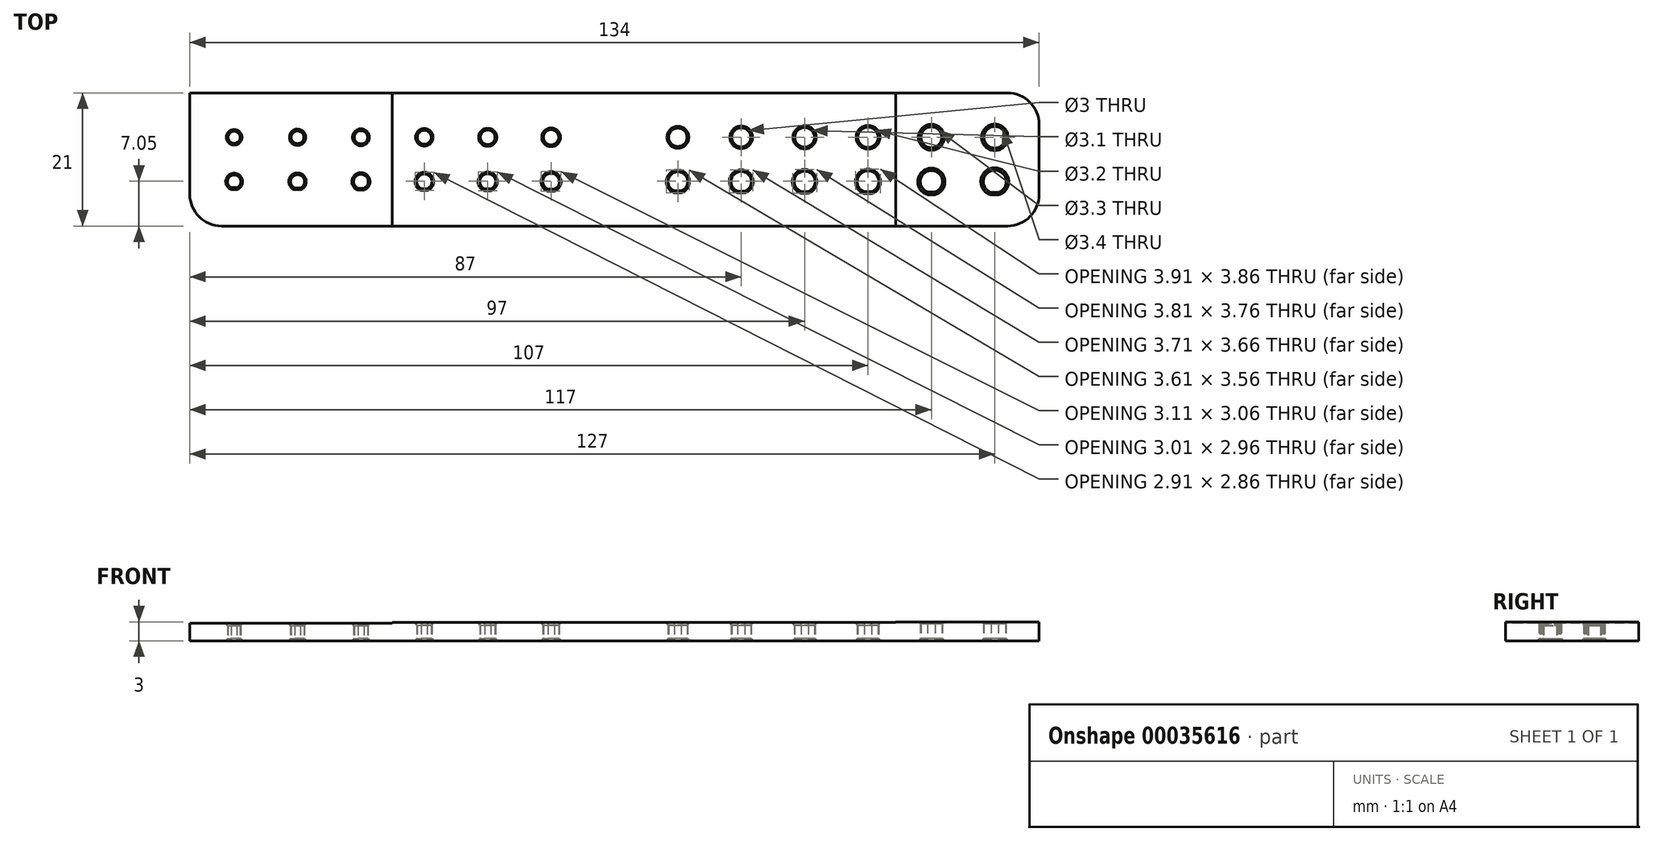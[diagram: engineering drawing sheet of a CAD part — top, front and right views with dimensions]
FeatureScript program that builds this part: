
annotation { "Feature Type Name" : "Feature", "Feature Type Description" : "" }
export const myFeature = defineFeature(function(context is Context, id is Id, definition is map)
    precondition{}
    {
        {
            var Q0;
            Q0=qCreatedBy(makeId("Top.planeOp"),FACE);
            var sketch = newSketch(context, id + "F0", { "sketchPlane" : qUnion([Q0])});
            skPoint(sketch, "E0.rect.middle", {"position": v(0, 0) * mm});
            skCircle(sketch, "E1", {"center": v(-50, 0) * mm, "radius": 1 * mm});
            skCircle(sketch, "E2", {"center": v(-40, 0) * mm, "radius": 1.05 * mm});
            skCircle(sketch, "E3", {"center": v(-30, 0) * mm, "radius": 1.1 * mm});
            skCircle(sketch, "E4", {"center": v(-20, 0) * mm, "radius": 1.15 * mm});
            skCircle(sketch, "E5", {"center": v(-10, 0) * mm, "radius": 1.2 * mm});
            skCircle(sketch, "E6", {"center": v(10, 0) * mm, "radius": 1.45 * mm});
            skCircle(sketch, "E7", {"center": v(20, 0) * mm, "radius": 1.5 * mm});
            skCircle(sketch, "E8", {"center": v(30, 0) * mm, "radius": 1.55 * mm});
            skCircle(sketch, "E9", {"center": v(40, 0) * mm, "radius": 1.6 * mm});
            skCircle(sketch, "E10", {"center": v(50, 0) * mm, "radius": 1.65 * mm});
            skCircle(sketch, "E11", {"center": v(60, 0) * mm, "radius": 1.7 * mm});
            skCircle(sketch, "E12", {"center": v(-60, 0) * mm, "radius": 0.95 * mm});
            skCircle(sketch, "E13", {"center": v(-30, -7) * mm, "radius": 1.2 * mm});
            skCircle(sketch, "E14", {"center": v(-20, -7) * mm, "radius": 1.25 * mm});
            skCircle(sketch, "E15", {"center": v(-10, -7) * mm, "radius": 1.3 * mm});
            skCircle(sketch, "E16", {"center": v(-40, -7) * mm, "radius": 1.15 * mm});
            skCircle(sketch, "E17", {"center": v(-50, -7) * mm, "radius": 1.1 * mm});
            skCircle(sketch, "E18", {"center": v(10, -7) * mm, "radius": 1.55 * mm});
            skPoint(sketch, "E19.rect.middle", {"position": v(0, -7) * mm});
            skCircle(sketch, "E20", {"center": v(20, -7) * mm, "radius": 1.6 * mm});
            skCircle(sketch, "E21", {"center": v(30, -7) * mm, "radius": 1.65 * mm});
            skCircle(sketch, "E22", {"center": v(40, -7) * mm, "radius": 1.7 * mm});
            skCircle(sketch, "E23", {"center": v(50, -7) * mm, "radius": 1.75 * mm});
            skCircle(sketch, "E24", {"center": v(60, -7) * mm, "radius": 1.8 * mm});
            skCircle(sketch, "E25", {"center": v(-60, -7) * mm, "radius": 1.05 * mm});
            skLineSegment(sketch, "E26.bottom", {"start": v(-67, 7) * mm, "end": v(67, 7) * mm});
            skLineSegment(sketch, "E26.top", {"start": v(-67, -14) * mm, "end": v(67, -14) * mm});
            skLineSegment(sketch, "E26.left", {"start": v(-67, 7) * mm, "end": v(-67, -14) * mm});
            skLineSegment(sketch, "E26.right", {"start": v(67, 7) * mm, "end": v(67, -14) * mm});
            skLineSegment(sketch, "E27", {"start": v(-60.45, -7.95) * mm, "end": v(-59.55, -7.95) * mm});
            skLineSegment(sketch, "E28", {"start": v(-50.46, -8) * mm, "end": v(-49.54, -8) * mm});
            skLineSegment(sketch, "E29", {"start": v(-40.47, -8.05) * mm, "end": v(-39.53, -8.05) * mm});
            skLineSegment(sketch, "E30", {"start": v(-30.48, -8.1) * mm, "end": v(-29.52, -8.1) * mm});
            skLineSegment(sketch, "E31", {"start": v(-20.49, -8.15) * mm, "end": v(-19.51, -8.15) * mm});
            skLineSegment(sketch, "E32", {"start": v(-10.5, -8.2) * mm, "end": v(-9.5, -8.2) * mm});
            skLineSegment(sketch, "E33", {"start": v(9.45, -8.45) * mm, "end": v(10.55, -8.45) * mm});
            skLineSegment(sketch, "E34", {"start": v(19.44, -8.5) * mm, "end": v(20.56, -8.5) * mm});
            skLineSegment(sketch, "E35", {"start": v(29.43, -8.55) * mm, "end": v(30.57, -8.55) * mm});
            skLineSegment(sketch, "E36", {"start": v(39.43, -8.6) * mm, "end": v(40.57, -8.6) * mm});
            skLineSegment(sketch, "E37", {"start": v(49.42, -8.65) * mm, "end": v(50.58, -8.65) * mm});
            skLineSegment(sketch, "E38", {"start": v(59.4, -8.7) * mm, "end": v(60.6, -8.7) * mm});
            skSolve(sketch);
        }
        {
            var Q0;
            {var subQ0=sQuery(id+"F0.wireOp",EDGE,"E27");Q0=makeQuery(id+"F0.imprint","IMPRINT",FACE,{"disambiguationData":[TD([[makeQuery(id+"F0.imprint","IMPRINT",EDGE,{"derivedFrom":subQ0}),-1.0]])]});}
            var Q1;
            {var subQ0=sQuery(id+"F0.wireOp",EDGE,"E28");Q1=makeQuery(id+"F0.imprint","IMPRINT",FACE,{"disambiguationData":[TD([[makeQuery(id+"F0.imprint","IMPRINT",EDGE,{"derivedFrom":subQ0}),-1.0]])]});}
            var Q2;
            {var subQ0=sQuery(id+"F0.wireOp",EDGE,"E29");Q2=makeQuery(id+"F0.imprint","IMPRINT",FACE,{"disambiguationData":[TD([[makeQuery(id+"F0.imprint","IMPRINT",EDGE,{"derivedFrom":subQ0}),-1.0]])]});}
            var Q3;
            {var subQ0=sQuery(id+"F0.wireOp",EDGE,"E30");Q3=makeQuery(id+"F0.imprint","IMPRINT",FACE,{"disambiguationData":[TD([[makeQuery(id+"F0.imprint","IMPRINT",EDGE,{"derivedFrom":subQ0}),-1.0]])]});}
            var Q4;
            {var subQ0=sQuery(id+"F0.wireOp",EDGE,"E31");Q4=makeQuery(id+"F0.imprint","IMPRINT",FACE,{"disambiguationData":[TD([[makeQuery(id+"F0.imprint","IMPRINT",EDGE,{"derivedFrom":subQ0}),-1.0]])]});}
            var Q5;
            {var subQ0=sQuery(id+"F0.wireOp",EDGE,"E32");Q5=makeQuery(id+"F0.imprint","IMPRINT",FACE,{"disambiguationData":[TD([[makeQuery(id+"F0.imprint","IMPRINT",EDGE,{"derivedFrom":subQ0}),-1.0]])]});}
            var Q6;
            {var subQ0=sQuery(id+"F0.wireOp",EDGE,"E33");Q6=makeQuery(id+"F0.imprint","IMPRINT",FACE,{"disambiguationData":[TD([[makeQuery(id+"F0.imprint","IMPRINT",EDGE,{"derivedFrom":subQ0}),-1.0]])]});}
            var Q7;
            {var subQ0=sQuery(id+"F0.wireOp",EDGE,"E34");Q7=makeQuery(id+"F0.imprint","IMPRINT",FACE,{"disambiguationData":[TD([[makeQuery(id+"F0.imprint","IMPRINT",EDGE,{"derivedFrom":subQ0}),-1.0]])]});}
            var Q8;
            Q8=makeQuery(id+"F0.imprint","IMPRINT",FACE,{"disambiguationData":[TD([[makeQuery(id+"F0.imprint","IMPRINT",EDGE,{"derivedFrom":sQuery(id+"F0.wireOp",EDGE,"E1")}),-1.0]])]});
            var Q9;
            {var subQ0=sQuery(id+"F0.wireOp",EDGE,"E35");Q9=makeQuery(id+"F0.imprint","IMPRINT",FACE,{"disambiguationData":[TD([[makeQuery(id+"F0.imprint","IMPRINT",EDGE,{"derivedFrom":subQ0}),-1.0]])]});}
            var Q10;
            {var subQ0=sQuery(id+"F0.wireOp",EDGE,"E36");Q10=makeQuery(id+"F0.imprint","IMPRINT",FACE,{"disambiguationData":[TD([[makeQuery(id+"F0.imprint","IMPRINT",EDGE,{"derivedFrom":subQ0}),-1.0]])]});}
            var Q11;
            {var subQ0=sQuery(id+"F0.wireOp",EDGE,"E37");Q11=makeQuery(id+"F0.imprint","IMPRINT",FACE,{"disambiguationData":[TD([[makeQuery(id+"F0.imprint","IMPRINT",EDGE,{"derivedFrom":subQ0}),-1.0]])]});}
            var Q12;
            {var subQ0=sQuery(id+"F0.wireOp",EDGE,"E38");Q12=makeQuery(id+"F0.imprint","IMPRINT",FACE,{"disambiguationData":[TD([[makeQuery(id+"F0.imprint","IMPRINT",EDGE,{"derivedFrom":subQ0}),-1.0]])]});}
            extrude(context, id + "F1", {"entities" : qUnion([Q0, Q1, Q2, Q3, Q4, Q5, Q6, Q7, Q8, Q9, Q10, Q11, Q12]), "depth" : 3 * mm});
        }
        {
            var Q0;
            Q0=makeQuery(id+"F1.opExtrude","CAP_FACE",FACE,{"disambiguationData":[OSD([sQuery(id+"F0.wireOp",EDGE,"E0.rect.bottom"),sQuery(id+"F0.wireOp",EDGE,"E0.rect.top"),sQuery(id+"F0.wireOp",EDGE,"E0.rect.left"),sQuery(id+"F0.wireOp",EDGE,"E0.rect.right"),sQuery(id+"F0.wireOp",EDGE,"E1"),sQuery(id+"F0.wireOp",EDGE,"E2"),sQuery(id+"F0.wireOp",EDGE,"E3"),sQuery(id+"F0.wireOp",EDGE,"E4"),sQuery(id+"F0.wireOp",EDGE,"E5"),sQuery(id+"F0.wireOp",EDGE,"E6"),sQuery(id+"F0.wireOp",EDGE,"E7"),sQuery(id+"F0.wireOp",EDGE,"E8"),sQuery(id+"F0.wireOp",EDGE,"E9"),sQuery(id+"F0.wireOp",EDGE,"E10"),sQuery(id+"F0.wireOp",EDGE,"E11"),sQuery(id+"F0.wireOp",EDGE,"E12")])],"isStart":false});
            var sketch = newSketch(context, id + "F2", { "sketchPlane" : qUnion([Q0])});
            skLineSegment(sketch, "E39.rect.bottom", {"start": v(44.35, -20.42) * mm, "end": v(-71, -20.42) * mm});
            skLineSegment(sketch, "E39.rect.top", {"start": v(44.35, 10.73) * mm, "end": v(-71, 10.73) * mm});
            skLineSegment(sketch, "E39.rect.left", {"start": v(44.35, -20.42) * mm, "end": v(44.35, 10.73) * mm});
            skLineSegment(sketch, "E39.rect.right", {"start": v(-71, -20.42) * mm, "end": v(-71, 10.73) * mm});
            skPoint(sketch, "E39.rect.middle", {"position": v(-13.32, -4.84) * mm});
            skSolve(sketch);
        }
        {
            var Q0;
            Q0 = qSketchRegion(id + "F2", true);
            extrude(context, id + "F3", {"entities" : qUnion([Q0]), "operationType" : NewBodyOperationType.REMOVE, "oppositeDirection" : true, "depth" : .1 * mm});
        }
        {
            var Q0;
            Q0=makeQuery(id+"F3.boolean.opBoolean","COPY",FACE,{"derivedFrom":makeQuery(id+"F3.opExtrude","CAP_FACE",FACE,{"disambiguationData":[OSD([sQuery(id+"F2.wireOp",EDGE,"E39.rect.bottom"),sQuery(id+"F2.wireOp",EDGE,"E39.rect.top"),sQuery(id+"F2.wireOp",EDGE,"E39.rect.left"),sQuery(id+"F2.wireOp",EDGE,"E39.rect.right")])],"isStart":false})});
            var sketch = newSketch(context, id + "F4", { "sketchPlane" : qUnion([Q0])});
            skLineSegment(sketch, "E40.bottom", {"start": v(-72.45, 11.13) * mm, "end": v(-35.06, 11.13) * mm});
            skLineSegment(sketch, "E40.top", {"start": v(-72.45, -20.3) * mm, "end": v(-35.06, -20.3) * mm});
            skLineSegment(sketch, "E40.left", {"start": v(-72.45, 11.13) * mm, "end": v(-72.45, -20.3) * mm});
            skLineSegment(sketch, "E40.right", {"start": v(-35.06, 11.13) * mm, "end": v(-35.06, -20.3) * mm});
            skSolve(sketch);
        }
        {
            var Q0;
            Q0 = qSketchRegion(id + "F4", true);
            extrude(context, id + "F5", {"entities" : qUnion([Q0]), "operationType" : NewBodyOperationType.REMOVE, "oppositeDirection" : true, "depth" : .1 * mm});
        }
        {
            var Q0;
            Q0=makeQuery(id+"F1.opExtrude","SWEPT_EDGE",EDGE,{"disambiguationData":[OSD([sQuery(id+"F0.wireOp",EDGE,"E26.top"),sQuery(id+"F0.wireOp",EDGE,"E26.left")])]});
            var Q1;
            Q1=makeQuery(id+"F1.opExtrude","SWEPT_EDGE",EDGE,{"disambiguationData":[OSD([sQuery(id+"F0.wireOp",EDGE,"E26.top"),sQuery(id+"F0.wireOp",EDGE,"E26.right")])]});
            var Q2;
            Q2=makeQuery(id+"F1.opExtrude","SWEPT_EDGE",EDGE,{"disambiguationData":[OSD([sQuery(id+"F0.wireOp",EDGE,"E26.bottom"),sQuery(id+"F0.wireOp",EDGE,"E26.right")])]});
            fillet(context, id + "F6", {"entities" : qUnion([Q0, Q1, Q2]), "radius" : 5 * mm, "tangentPropagation" : true, "allowEdgeOverflow" : false});
        }
        {
            var Q0;
            Q0=makeQuery(id+"F5.boolean.opBoolean","INTERSECT",EDGE,{"derivedFrom":[makeQuery(id+"F1.opExtrude","SWEPT_FACE",FACE,{"disambiguationData":[OSD([sQuery(id+"F0.wireOp",EDGE,"E12")])]}),makeQuery(id+"F5.opExtrude","CAP_FACE",FACE,{"disambiguationData":[OSD([sQuery(id+"F4.wireOp",EDGE,"E40.bottom"),sQuery(id+"F4.wireOp",EDGE,"E40.top"),sQuery(id+"F4.wireOp",EDGE,"E40.left"),sQuery(id+"F4.wireOp",EDGE,"E40.right")])],"isStart":false})]});
            var Q1;
            Q1=makeQuery(id+"F5.boolean.opBoolean","INTERSECT",EDGE,{"derivedFrom":[makeQuery(id+"F1.opExtrude","SWEPT_FACE",FACE,{"disambiguationData":[OSD([sQuery(id+"F0.wireOp",EDGE,"E1")])]}),makeQuery(id+"F5.opExtrude","CAP_FACE",FACE,{"disambiguationData":[OSD([sQuery(id+"F4.wireOp",EDGE,"E40.bottom"),sQuery(id+"F4.wireOp",EDGE,"E40.top"),sQuery(id+"F4.wireOp",EDGE,"E40.left"),sQuery(id+"F4.wireOp",EDGE,"E40.right")])],"isStart":false})]});
            var Q2;
            Q2=makeQuery(id+"F5.boolean.opBoolean","INTERSECT",EDGE,{"derivedFrom":[makeQuery(id+"F1.opExtrude","SWEPT_FACE",FACE,{"disambiguationData":[OSD([sQuery(id+"F0.wireOp",EDGE,"E25")])]}),makeQuery(id+"F5.opExtrude","CAP_FACE",FACE,{"disambiguationData":[OSD([sQuery(id+"F4.wireOp",EDGE,"E40.bottom"),sQuery(id+"F4.wireOp",EDGE,"E40.top"),sQuery(id+"F4.wireOp",EDGE,"E40.left"),sQuery(id+"F4.wireOp",EDGE,"E40.right")])],"isStart":false})]});
            var Q3;
            Q3=makeQuery(id+"F5.boolean.opBoolean","INTERSECT",EDGE,{"derivedFrom":[makeQuery(id+"F1.opExtrude","SWEPT_FACE",FACE,{"disambiguationData":[OSD([sQuery(id+"F0.wireOp",EDGE,"E27")])]}),makeQuery(id+"F5.opExtrude","CAP_FACE",FACE,{"disambiguationData":[OSD([sQuery(id+"F4.wireOp",EDGE,"E40.bottom"),sQuery(id+"F4.wireOp",EDGE,"E40.top"),sQuery(id+"F4.wireOp",EDGE,"E40.left"),sQuery(id+"F4.wireOp",EDGE,"E40.right")])],"isStart":false})]});
            var Q4;
            Q4=makeQuery(id+"F5.boolean.opBoolean","INTERSECT",EDGE,{"derivedFrom":[makeQuery(id+"F1.opExtrude","SWEPT_FACE",FACE,{"disambiguationData":[OSD([sQuery(id+"F0.wireOp",EDGE,"E28")])]}),makeQuery(id+"F5.opExtrude","CAP_FACE",FACE,{"disambiguationData":[OSD([sQuery(id+"F4.wireOp",EDGE,"E40.bottom"),sQuery(id+"F4.wireOp",EDGE,"E40.top"),sQuery(id+"F4.wireOp",EDGE,"E40.left"),sQuery(id+"F4.wireOp",EDGE,"E40.right")])],"isStart":false})]});
            var Q5;
            Q5=makeQuery(id+"F5.boolean.opBoolean","INTERSECT",EDGE,{"derivedFrom":[makeQuery(id+"F1.opExtrude","SWEPT_FACE",FACE,{"disambiguationData":[OSD([sQuery(id+"F0.wireOp",EDGE,"E17")])]}),makeQuery(id+"F5.opExtrude","CAP_FACE",FACE,{"disambiguationData":[OSD([sQuery(id+"F4.wireOp",EDGE,"E40.bottom"),sQuery(id+"F4.wireOp",EDGE,"E40.top"),sQuery(id+"F4.wireOp",EDGE,"E40.left"),sQuery(id+"F4.wireOp",EDGE,"E40.right")])],"isStart":false})]});
            var Q6;
            Q6=makeQuery(id+"F5.boolean.opBoolean","INTERSECT",EDGE,{"derivedFrom":[makeQuery(id+"F1.opExtrude","SWEPT_FACE",FACE,{"disambiguationData":[OSD([sQuery(id+"F0.wireOp",EDGE,"E2")])]}),makeQuery(id+"F5.opExtrude","CAP_FACE",FACE,{"disambiguationData":[OSD([sQuery(id+"F4.wireOp",EDGE,"E40.bottom"),sQuery(id+"F4.wireOp",EDGE,"E40.top"),sQuery(id+"F4.wireOp",EDGE,"E40.left"),sQuery(id+"F4.wireOp",EDGE,"E40.right")])],"isStart":false})]});
            var Q7;
            Q7=makeQuery(id+"F5.boolean.opBoolean","INTERSECT",EDGE,{"derivedFrom":[makeQuery(id+"F1.opExtrude","SWEPT_FACE",FACE,{"disambiguationData":[OSD([sQuery(id+"F0.wireOp",EDGE,"E29")])]}),makeQuery(id+"F5.opExtrude","CAP_FACE",FACE,{"disambiguationData":[OSD([sQuery(id+"F4.wireOp",EDGE,"E40.bottom"),sQuery(id+"F4.wireOp",EDGE,"E40.top"),sQuery(id+"F4.wireOp",EDGE,"E40.left"),sQuery(id+"F4.wireOp",EDGE,"E40.right")])],"isStart":false})]});
            var Q8;
            Q8=makeQuery(id+"F5.boolean.opBoolean","INTERSECT",EDGE,{"derivedFrom":[makeQuery(id+"F1.opExtrude","SWEPT_FACE",FACE,{"disambiguationData":[OSD([sQuery(id+"F0.wireOp",EDGE,"E16")])]}),makeQuery(id+"F5.opExtrude","CAP_FACE",FACE,{"disambiguationData":[OSD([sQuery(id+"F4.wireOp",EDGE,"E40.bottom"),sQuery(id+"F4.wireOp",EDGE,"E40.top"),sQuery(id+"F4.wireOp",EDGE,"E40.left"),sQuery(id+"F4.wireOp",EDGE,"E40.right")])],"isStart":false})]});
            var Q9;
            Q9=makeQuery(id+"F3.boolean.opBoolean","INTERSECT",EDGE,{"derivedFrom":[makeQuery(id+"F1.opExtrude","SWEPT_FACE",FACE,{"disambiguationData":[OSD([sQuery(id+"F0.wireOp",EDGE,"E3")])]}),makeQuery(id+"F3.opExtrude","CAP_FACE",FACE,{"disambiguationData":[OSD([sQuery(id+"F2.wireOp",EDGE,"E39.rect.bottom"),sQuery(id+"F2.wireOp",EDGE,"E39.rect.top"),sQuery(id+"F2.wireOp",EDGE,"E39.rect.left"),sQuery(id+"F2.wireOp",EDGE,"E39.rect.right")])],"isStart":false})]});
            var Q10;
            Q10=makeQuery(id+"F3.boolean.opBoolean","INTERSECT",EDGE,{"derivedFrom":[makeQuery(id+"F1.opExtrude","SWEPT_FACE",FACE,{"disambiguationData":[OSD([sQuery(id+"F0.wireOp",EDGE,"E30")])]}),makeQuery(id+"F3.opExtrude","CAP_FACE",FACE,{"disambiguationData":[OSD([sQuery(id+"F2.wireOp",EDGE,"E39.rect.bottom"),sQuery(id+"F2.wireOp",EDGE,"E39.rect.top"),sQuery(id+"F2.wireOp",EDGE,"E39.rect.left"),sQuery(id+"F2.wireOp",EDGE,"E39.rect.right")])],"isStart":false})]});
            var Q11;
            Q11=makeQuery(id+"F3.boolean.opBoolean","INTERSECT",EDGE,{"derivedFrom":[makeQuery(id+"F1.opExtrude","SWEPT_FACE",FACE,{"disambiguationData":[OSD([sQuery(id+"F0.wireOp",EDGE,"E13")])]}),makeQuery(id+"F3.opExtrude","CAP_FACE",FACE,{"disambiguationData":[OSD([sQuery(id+"F2.wireOp",EDGE,"E39.rect.bottom"),sQuery(id+"F2.wireOp",EDGE,"E39.rect.top"),sQuery(id+"F2.wireOp",EDGE,"E39.rect.left"),sQuery(id+"F2.wireOp",EDGE,"E39.rect.right")])],"isStart":false})]});
            var Q12;
            Q12=makeQuery(id+"F3.boolean.opBoolean","INTERSECT",EDGE,{"derivedFrom":[makeQuery(id+"F1.opExtrude","SWEPT_FACE",FACE,{"disambiguationData":[OSD([sQuery(id+"F0.wireOp",EDGE,"E4")])]}),makeQuery(id+"F3.opExtrude","CAP_FACE",FACE,{"disambiguationData":[OSD([sQuery(id+"F2.wireOp",EDGE,"E39.rect.bottom"),sQuery(id+"F2.wireOp",EDGE,"E39.rect.top"),sQuery(id+"F2.wireOp",EDGE,"E39.rect.left"),sQuery(id+"F2.wireOp",EDGE,"E39.rect.right")])],"isStart":false})]});
            var Q13;
            Q13=makeQuery(id+"F3.boolean.opBoolean","INTERSECT",EDGE,{"derivedFrom":[makeQuery(id+"F1.opExtrude","SWEPT_FACE",FACE,{"disambiguationData":[OSD([sQuery(id+"F0.wireOp",EDGE,"E31")])]}),makeQuery(id+"F3.opExtrude","CAP_FACE",FACE,{"disambiguationData":[OSD([sQuery(id+"F2.wireOp",EDGE,"E39.rect.bottom"),sQuery(id+"F2.wireOp",EDGE,"E39.rect.top"),sQuery(id+"F2.wireOp",EDGE,"E39.rect.left"),sQuery(id+"F2.wireOp",EDGE,"E39.rect.right")])],"isStart":false})]});
            var Q14;
            Q14=makeQuery(id+"F3.boolean.opBoolean","INTERSECT",EDGE,{"derivedFrom":[makeQuery(id+"F1.opExtrude","SWEPT_FACE",FACE,{"disambiguationData":[OSD([sQuery(id+"F0.wireOp",EDGE,"E14")])]}),makeQuery(id+"F3.opExtrude","CAP_FACE",FACE,{"disambiguationData":[OSD([sQuery(id+"F2.wireOp",EDGE,"E39.rect.bottom"),sQuery(id+"F2.wireOp",EDGE,"E39.rect.top"),sQuery(id+"F2.wireOp",EDGE,"E39.rect.left"),sQuery(id+"F2.wireOp",EDGE,"E39.rect.right")])],"isStart":false})]});
            var Q15;
            Q15=makeQuery(id+"F3.boolean.opBoolean","INTERSECT",EDGE,{"derivedFrom":[makeQuery(id+"F1.opExtrude","SWEPT_FACE",FACE,{"disambiguationData":[OSD([sQuery(id+"F0.wireOp",EDGE,"E5")])]}),makeQuery(id+"F3.opExtrude","CAP_FACE",FACE,{"disambiguationData":[OSD([sQuery(id+"F2.wireOp",EDGE,"E39.rect.bottom"),sQuery(id+"F2.wireOp",EDGE,"E39.rect.top"),sQuery(id+"F2.wireOp",EDGE,"E39.rect.left"),sQuery(id+"F2.wireOp",EDGE,"E39.rect.right")])],"isStart":false})]});
            var Q16;
            Q16=makeQuery(id+"F3.boolean.opBoolean","INTERSECT",EDGE,{"derivedFrom":[makeQuery(id+"F1.opExtrude","SWEPT_FACE",FACE,{"disambiguationData":[OSD([sQuery(id+"F0.wireOp",EDGE,"E32")])]}),makeQuery(id+"F3.opExtrude","CAP_FACE",FACE,{"disambiguationData":[OSD([sQuery(id+"F2.wireOp",EDGE,"E39.rect.bottom"),sQuery(id+"F2.wireOp",EDGE,"E39.rect.top"),sQuery(id+"F2.wireOp",EDGE,"E39.rect.left"),sQuery(id+"F2.wireOp",EDGE,"E39.rect.right")])],"isStart":false})]});
            var Q17;
            Q17=makeQuery(id+"F3.boolean.opBoolean","INTERSECT",EDGE,{"derivedFrom":[makeQuery(id+"F1.opExtrude","SWEPT_FACE",FACE,{"disambiguationData":[OSD([sQuery(id+"F0.wireOp",EDGE,"E15")])]}),makeQuery(id+"F3.opExtrude","CAP_FACE",FACE,{"disambiguationData":[OSD([sQuery(id+"F2.wireOp",EDGE,"E39.rect.bottom"),sQuery(id+"F2.wireOp",EDGE,"E39.rect.top"),sQuery(id+"F2.wireOp",EDGE,"E39.rect.left"),sQuery(id+"F2.wireOp",EDGE,"E39.rect.right")])],"isStart":false})]});
            var Q18;
            Q18=makeQuery(id+"F3.boolean.opBoolean","INTERSECT",EDGE,{"derivedFrom":[makeQuery(id+"F1.opExtrude","SWEPT_FACE",FACE,{"disambiguationData":[OSD([sQuery(id+"F0.wireOp",EDGE,"E33")])]}),makeQuery(id+"F3.opExtrude","CAP_FACE",FACE,{"disambiguationData":[OSD([sQuery(id+"F2.wireOp",EDGE,"E39.rect.bottom"),sQuery(id+"F2.wireOp",EDGE,"E39.rect.top"),sQuery(id+"F2.wireOp",EDGE,"E39.rect.left"),sQuery(id+"F2.wireOp",EDGE,"E39.rect.right")])],"isStart":false})]});
            var Q19;
            Q19=makeQuery(id+"F3.boolean.opBoolean","INTERSECT",EDGE,{"derivedFrom":[makeQuery(id+"F1.opExtrude","SWEPT_FACE",FACE,{"disambiguationData":[OSD([sQuery(id+"F0.wireOp",EDGE,"E18")])]}),makeQuery(id+"F3.opExtrude","CAP_FACE",FACE,{"disambiguationData":[OSD([sQuery(id+"F2.wireOp",EDGE,"E39.rect.bottom"),sQuery(id+"F2.wireOp",EDGE,"E39.rect.top"),sQuery(id+"F2.wireOp",EDGE,"E39.rect.left"),sQuery(id+"F2.wireOp",EDGE,"E39.rect.right")])],"isStart":false})]});
            var Q20;
            Q20=makeQuery(id+"F3.boolean.opBoolean","INTERSECT",EDGE,{"derivedFrom":[makeQuery(id+"F1.opExtrude","SWEPT_FACE",FACE,{"disambiguationData":[OSD([sQuery(id+"F0.wireOp",EDGE,"E6")])]}),makeQuery(id+"F3.opExtrude","CAP_FACE",FACE,{"disambiguationData":[OSD([sQuery(id+"F2.wireOp",EDGE,"E39.rect.bottom"),sQuery(id+"F2.wireOp",EDGE,"E39.rect.top"),sQuery(id+"F2.wireOp",EDGE,"E39.rect.left"),sQuery(id+"F2.wireOp",EDGE,"E39.rect.right")])],"isStart":false})]});
            var Q21;
            Q21=makeQuery(id+"F3.boolean.opBoolean","INTERSECT",EDGE,{"derivedFrom":[makeQuery(id+"F1.opExtrude","SWEPT_FACE",FACE,{"disambiguationData":[OSD([sQuery(id+"F0.wireOp",EDGE,"E34")])]}),makeQuery(id+"F3.opExtrude","CAP_FACE",FACE,{"disambiguationData":[OSD([sQuery(id+"F2.wireOp",EDGE,"E39.rect.bottom"),sQuery(id+"F2.wireOp",EDGE,"E39.rect.top"),sQuery(id+"F2.wireOp",EDGE,"E39.rect.left"),sQuery(id+"F2.wireOp",EDGE,"E39.rect.right")])],"isStart":false})]});
            var Q22;
            Q22=makeQuery(id+"F3.boolean.opBoolean","INTERSECT",EDGE,{"derivedFrom":[makeQuery(id+"F1.opExtrude","SWEPT_FACE",FACE,{"disambiguationData":[OSD([sQuery(id+"F0.wireOp",EDGE,"E20")])]}),makeQuery(id+"F3.opExtrude","CAP_FACE",FACE,{"disambiguationData":[OSD([sQuery(id+"F2.wireOp",EDGE,"E39.rect.bottom"),sQuery(id+"F2.wireOp",EDGE,"E39.rect.top"),sQuery(id+"F2.wireOp",EDGE,"E39.rect.left"),sQuery(id+"F2.wireOp",EDGE,"E39.rect.right")])],"isStart":false})]});
            var Q23;
            Q23=makeQuery(id+"F3.boolean.opBoolean","INTERSECT",EDGE,{"derivedFrom":[makeQuery(id+"F1.opExtrude","SWEPT_FACE",FACE,{"disambiguationData":[OSD([sQuery(id+"F0.wireOp",EDGE,"E7")])]}),makeQuery(id+"F3.opExtrude","CAP_FACE",FACE,{"disambiguationData":[OSD([sQuery(id+"F2.wireOp",EDGE,"E39.rect.bottom"),sQuery(id+"F2.wireOp",EDGE,"E39.rect.top"),sQuery(id+"F2.wireOp",EDGE,"E39.rect.left"),sQuery(id+"F2.wireOp",EDGE,"E39.rect.right")])],"isStart":false})]});
            var Q24;
            Q24=makeQuery(id+"F3.boolean.opBoolean","INTERSECT",EDGE,{"derivedFrom":[makeQuery(id+"F1.opExtrude","SWEPT_FACE",FACE,{"disambiguationData":[OSD([sQuery(id+"F0.wireOp",EDGE,"E35")])]}),makeQuery(id+"F3.opExtrude","CAP_FACE",FACE,{"disambiguationData":[OSD([sQuery(id+"F2.wireOp",EDGE,"E39.rect.bottom"),sQuery(id+"F2.wireOp",EDGE,"E39.rect.top"),sQuery(id+"F2.wireOp",EDGE,"E39.rect.left"),sQuery(id+"F2.wireOp",EDGE,"E39.rect.right")])],"isStart":false})]});
            var Q25;
            Q25=makeQuery(id+"F3.boolean.opBoolean","INTERSECT",EDGE,{"derivedFrom":[makeQuery(id+"F1.opExtrude","SWEPT_FACE",FACE,{"disambiguationData":[OSD([sQuery(id+"F0.wireOp",EDGE,"E21")])]}),makeQuery(id+"F3.opExtrude","CAP_FACE",FACE,{"disambiguationData":[OSD([sQuery(id+"F2.wireOp",EDGE,"E39.rect.bottom"),sQuery(id+"F2.wireOp",EDGE,"E39.rect.top"),sQuery(id+"F2.wireOp",EDGE,"E39.rect.left"),sQuery(id+"F2.wireOp",EDGE,"E39.rect.right")])],"isStart":false})]});
            var Q26;
            Q26=makeQuery(id+"F3.boolean.opBoolean","INTERSECT",EDGE,{"derivedFrom":[makeQuery(id+"F1.opExtrude","SWEPT_FACE",FACE,{"disambiguationData":[OSD([sQuery(id+"F0.wireOp",EDGE,"E8")])]}),makeQuery(id+"F3.opExtrude","CAP_FACE",FACE,{"disambiguationData":[OSD([sQuery(id+"F2.wireOp",EDGE,"E39.rect.bottom"),sQuery(id+"F2.wireOp",EDGE,"E39.rect.top"),sQuery(id+"F2.wireOp",EDGE,"E39.rect.left"),sQuery(id+"F2.wireOp",EDGE,"E39.rect.right")])],"isStart":false})]});
            var Q27;
            Q27=makeQuery(id+"F3.boolean.opBoolean","INTERSECT",EDGE,{"derivedFrom":[makeQuery(id+"F1.opExtrude","SWEPT_FACE",FACE,{"disambiguationData":[OSD([sQuery(id+"F0.wireOp",EDGE,"E36")])]}),makeQuery(id+"F3.opExtrude","CAP_FACE",FACE,{"disambiguationData":[OSD([sQuery(id+"F2.wireOp",EDGE,"E39.rect.bottom"),sQuery(id+"F2.wireOp",EDGE,"E39.rect.top"),sQuery(id+"F2.wireOp",EDGE,"E39.rect.left"),sQuery(id+"F2.wireOp",EDGE,"E39.rect.right")])],"isStart":false})]});
            var Q28;
            Q28=makeQuery(id+"F3.boolean.opBoolean","INTERSECT",EDGE,{"derivedFrom":[makeQuery(id+"F1.opExtrude","SWEPT_FACE",FACE,{"disambiguationData":[OSD([sQuery(id+"F0.wireOp",EDGE,"E22")])]}),makeQuery(id+"F3.opExtrude","CAP_FACE",FACE,{"disambiguationData":[OSD([sQuery(id+"F2.wireOp",EDGE,"E39.rect.bottom"),sQuery(id+"F2.wireOp",EDGE,"E39.rect.top"),sQuery(id+"F2.wireOp",EDGE,"E39.rect.left"),sQuery(id+"F2.wireOp",EDGE,"E39.rect.right")])],"isStart":false})]});
            var Q29;
            Q29=makeQuery(id+"F3.boolean.opBoolean","INTERSECT",EDGE,{"derivedFrom":[makeQuery(id+"F1.opExtrude","SWEPT_FACE",FACE,{"disambiguationData":[OSD([sQuery(id+"F0.wireOp",EDGE,"E9")])]}),makeQuery(id+"F3.opExtrude","CAP_FACE",FACE,{"disambiguationData":[OSD([sQuery(id+"F2.wireOp",EDGE,"E39.rect.bottom"),sQuery(id+"F2.wireOp",EDGE,"E39.rect.top"),sQuery(id+"F2.wireOp",EDGE,"E39.rect.left"),sQuery(id+"F2.wireOp",EDGE,"E39.rect.right")])],"isStart":false})]});
            var Q30;
            Q30=makeQuery(id+"F1.opExtrude","CAP_EDGE",EDGE,{"disambiguationData":[OSD([sQuery(id+"F0.wireOp",EDGE,"E37")])],"isStart":false});
            var Q31;
            Q31=makeQuery(id+"F1.opExtrude","CAP_EDGE",EDGE,{"disambiguationData":[OSD([sQuery(id+"F0.wireOp",EDGE,"E23")])],"isStart":false});
            var Q32;
            Q32=makeQuery(id+"F1.opExtrude","CAP_EDGE",EDGE,{"disambiguationData":[OSD([sQuery(id+"F0.wireOp",EDGE,"E10")])],"isStart":false});
            var Q33;
            Q33=makeQuery(id+"F1.opExtrude","CAP_EDGE",EDGE,{"disambiguationData":[OSD([sQuery(id+"F0.wireOp",EDGE,"E38")])],"isStart":false});
            var Q34;
            Q34=makeQuery(id+"F1.opExtrude","CAP_EDGE",EDGE,{"disambiguationData":[OSD([sQuery(id+"F0.wireOp",EDGE,"E24")])],"isStart":false});
            var Q35;
            Q35=makeQuery(id+"F1.opExtrude","CAP_EDGE",EDGE,{"disambiguationData":[OSD([sQuery(id+"F0.wireOp",EDGE,"E11")])],"isStart":false});
            chamfer(context, id + "F7", {"entities" : qUnion([Q0, Q1, Q2, Q3, Q4, Q5, Q6, Q7, Q8, Q9, Q10, Q11, Q12, Q13, Q14, Q15, Q16, Q17, Q18, Q19, Q20, Q21, Q22, Q23, Q24, Q25, Q26, Q27, Q28, Q29, Q30, Q31, Q32, Q33, Q34, Q35]), "chamferType" : ChamferType.OFFSET_ANGLE, "width" : .4 * mm, "oppositeDirection" : false, "angle" : 35 * degree, "tangentPropagation" : true});
        }
        {
            var Q0;
            Q0=makeQuery(id+"F1.opExtrude","CAP_EDGE",EDGE,{"disambiguationData":[OSD([sQuery(id+"F0.wireOp",EDGE,"E11")])],"isStart":true});
            var Q1;
            Q1=makeQuery(id+"F1.opExtrude","CAP_EDGE",EDGE,{"disambiguationData":[OSD([sQuery(id+"F0.wireOp",EDGE,"E38")])],"isStart":true});
            var Q2;
            Q2=makeQuery(id+"F1.opExtrude","CAP_EDGE",EDGE,{"disambiguationData":[OSD([sQuery(id+"F0.wireOp",EDGE,"E24")])],"isStart":true});
            var Q3;
            Q3=makeQuery(id+"F1.opExtrude","CAP_EDGE",EDGE,{"disambiguationData":[OSD([sQuery(id+"F0.wireOp",EDGE,"E10")])],"isStart":true});
            var Q4;
            Q4=makeQuery(id+"F1.opExtrude","CAP_EDGE",EDGE,{"disambiguationData":[OSD([sQuery(id+"F0.wireOp",EDGE,"E37")])],"isStart":true});
            var Q5;
            Q5=makeQuery(id+"F1.opExtrude","CAP_EDGE",EDGE,{"disambiguationData":[OSD([sQuery(id+"F0.wireOp",EDGE,"E23")])],"isStart":true});
            var Q6;
            Q6=makeQuery(id+"F1.opExtrude","CAP_EDGE",EDGE,{"disambiguationData":[OSD([sQuery(id+"F0.wireOp",EDGE,"E36")])],"isStart":true});
            var Q7;
            Q7=makeQuery(id+"F1.opExtrude","CAP_EDGE",EDGE,{"disambiguationData":[OSD([sQuery(id+"F0.wireOp",EDGE,"E22")])],"isStart":true});
            var Q8;
            Q8=makeQuery(id+"F1.opExtrude","CAP_EDGE",EDGE,{"disambiguationData":[OSD([sQuery(id+"F0.wireOp",EDGE,"E9")])],"isStart":true});
            var Q9;
            Q9=makeQuery(id+"F1.opExtrude","CAP_EDGE",EDGE,{"disambiguationData":[OSD([sQuery(id+"F0.wireOp",EDGE,"E35")])],"isStart":true});
            var Q10;
            Q10=makeQuery(id+"F1.opExtrude","CAP_EDGE",EDGE,{"disambiguationData":[OSD([sQuery(id+"F0.wireOp",EDGE,"E21")])],"isStart":true});
            var Q11;
            Q11=makeQuery(id+"F1.opExtrude","CAP_EDGE",EDGE,{"disambiguationData":[OSD([sQuery(id+"F0.wireOp",EDGE,"E8")])],"isStart":true});
            var Q12;
            Q12=makeQuery(id+"F1.opExtrude","CAP_EDGE",EDGE,{"disambiguationData":[OSD([sQuery(id+"F0.wireOp",EDGE,"E34")])],"isStart":true});
            var Q13;
            Q13=makeQuery(id+"F1.opExtrude","CAP_EDGE",EDGE,{"disambiguationData":[OSD([sQuery(id+"F0.wireOp",EDGE,"E20")])],"isStart":true});
            var Q14;
            Q14=makeQuery(id+"F1.opExtrude","CAP_EDGE",EDGE,{"disambiguationData":[OSD([sQuery(id+"F0.wireOp",EDGE,"E7")])],"isStart":true});
            var Q15;
            Q15=makeQuery(id+"F1.opExtrude","CAP_EDGE",EDGE,{"disambiguationData":[OSD([sQuery(id+"F0.wireOp",EDGE,"E33")])],"isStart":true});
            var Q16;
            Q16=makeQuery(id+"F1.opExtrude","CAP_EDGE",EDGE,{"disambiguationData":[OSD([sQuery(id+"F0.wireOp",EDGE,"E18")])],"isStart":true});
            var Q17;
            Q17=makeQuery(id+"F1.opExtrude","CAP_EDGE",EDGE,{"disambiguationData":[OSD([sQuery(id+"F0.wireOp",EDGE,"E6")])],"isStart":true});
            var Q18;
            Q18=makeQuery(id+"F1.opExtrude","CAP_EDGE",EDGE,{"disambiguationData":[OSD([sQuery(id+"F0.wireOp",EDGE,"E32")])],"isStart":true});
            var Q19;
            Q19=makeQuery(id+"F1.opExtrude","CAP_EDGE",EDGE,{"disambiguationData":[OSD([sQuery(id+"F0.wireOp",EDGE,"E15")])],"isStart":true});
            var Q20;
            Q20=makeQuery(id+"F1.opExtrude","CAP_EDGE",EDGE,{"disambiguationData":[OSD([sQuery(id+"F0.wireOp",EDGE,"E5")])],"isStart":true});
            var Q21;
            Q21=makeQuery(id+"F1.opExtrude","CAP_EDGE",EDGE,{"disambiguationData":[OSD([sQuery(id+"F0.wireOp",EDGE,"E31")])],"isStart":true});
            var Q22;
            Q22=makeQuery(id+"F1.opExtrude","CAP_EDGE",EDGE,{"disambiguationData":[OSD([sQuery(id+"F0.wireOp",EDGE,"E14")])],"isStart":true});
            var Q23;
            Q23=makeQuery(id+"F1.opExtrude","CAP_EDGE",EDGE,{"disambiguationData":[OSD([sQuery(id+"F0.wireOp",EDGE,"E4")])],"isStart":true});
            var Q24;
            Q24=makeQuery(id+"F1.opExtrude","CAP_EDGE",EDGE,{"disambiguationData":[OSD([sQuery(id+"F0.wireOp",EDGE,"E30")])],"isStart":true});
            var Q25;
            Q25=makeQuery(id+"F1.opExtrude","CAP_EDGE",EDGE,{"disambiguationData":[OSD([sQuery(id+"F0.wireOp",EDGE,"E13")])],"isStart":true});
            var Q26;
            Q26=makeQuery(id+"F1.opExtrude","CAP_EDGE",EDGE,{"disambiguationData":[OSD([sQuery(id+"F0.wireOp",EDGE,"E3")])],"isStart":true});
            var Q27;
            Q27=makeQuery(id+"F1.opExtrude","CAP_EDGE",EDGE,{"disambiguationData":[OSD([sQuery(id+"F0.wireOp",EDGE,"E29")])],"isStart":true});
            var Q28;
            Q28=makeQuery(id+"F1.opExtrude","CAP_EDGE",EDGE,{"disambiguationData":[OSD([sQuery(id+"F0.wireOp",EDGE,"E16")])],"isStart":true});
            var Q29;
            Q29=makeQuery(id+"F1.opExtrude","CAP_EDGE",EDGE,{"disambiguationData":[OSD([sQuery(id+"F0.wireOp",EDGE,"E2")])],"isStart":true});
            var Q30;
            Q30=makeQuery(id+"F1.opExtrude","CAP_EDGE",EDGE,{"disambiguationData":[OSD([sQuery(id+"F0.wireOp",EDGE,"E1")])],"isStart":true});
            var Q31;
            Q31=makeQuery(id+"F1.opExtrude","CAP_EDGE",EDGE,{"disambiguationData":[OSD([sQuery(id+"F0.wireOp",EDGE,"E28")])],"isStart":true});
            var Q32;
            Q32=makeQuery(id+"F1.opExtrude","CAP_EDGE",EDGE,{"disambiguationData":[OSD([sQuery(id+"F0.wireOp",EDGE,"E17")])],"isStart":true});
            var Q33;
            Q33=makeQuery(id+"F1.opExtrude","CAP_EDGE",EDGE,{"disambiguationData":[OSD([sQuery(id+"F0.wireOp",EDGE,"E27")])],"isStart":true});
            var Q34;
            Q34=makeQuery(id+"F1.opExtrude","CAP_EDGE",EDGE,{"disambiguationData":[OSD([sQuery(id+"F0.wireOp",EDGE,"E25")])],"isStart":true});
            var Q35;
            Q35=makeQuery(id+"F1.opExtrude","CAP_EDGE",EDGE,{"disambiguationData":[OSD([sQuery(id+"F0.wireOp",EDGE,"E12")])],"isStart":true});
            chamfer(context, id + "F8", {"entities" : qUnion([Q0, Q1, Q2, Q3, Q4, Q5, Q6, Q7, Q8, Q9, Q10, Q11, Q12, Q13, Q14, Q15, Q16, Q17, Q18, Q19, Q20, Q21, Q22, Q23, Q24, Q25, Q26, Q27, Q28, Q29, Q30, Q31, Q32, Q33, Q34, Q35]), "chamferType" : ChamferType.OFFSET_ANGLE, "width" : .4 * mm, "oppositeDirection" : true, "angle" : 35 * degree, "tangentPropagation" : true});
        }
    });
